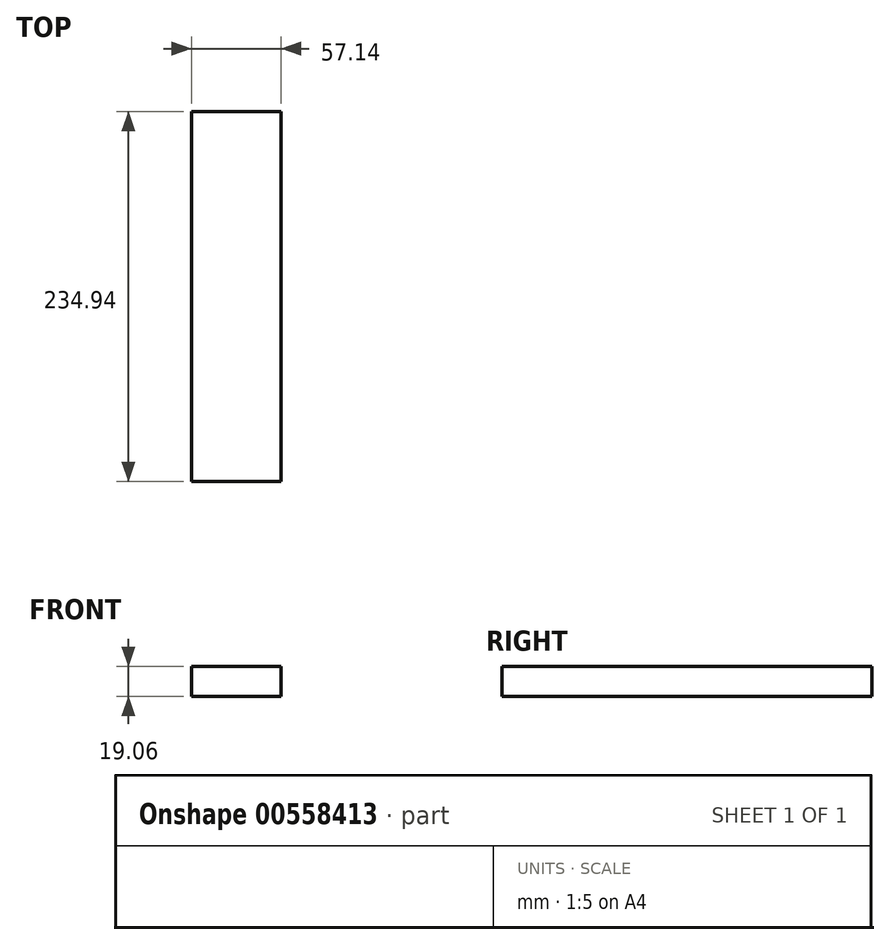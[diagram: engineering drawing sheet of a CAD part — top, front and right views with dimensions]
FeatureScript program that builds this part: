
annotation { "Feature Type Name" : "Feature", "Feature Type Description" : "" }
export const myFeature = defineFeature(function(context is Context, id is Id, definition is map)
    precondition{}
    {
        {
            var Q0;
            Q0=qCreatedBy(makeId("Top.planeOp"),FACE);
            var sketch = newSketch(context, id + "F0", { "sketchPlane" : qUnion([Q0])});
            skLineSegment(sketch, "E0.bottom", {"start": v(28.58, 117.47) * mm, "end": v(-28.57, 117.47) * mm});
            skLineSegment(sketch, "E0.top", {"start": v(28.57, -117.48) * mm, "end": v(-28.58, -117.48) * mm});
            skLineSegment(sketch, "E0.left", {"start": v(28.58, 117.47) * mm, "end": v(28.57, -117.48) * mm});
            skLineSegment(sketch, "E0.right", {"start": v(-28.57, 117.47) * mm, "end": v(-28.58, -117.48) * mm});
            skPoint(sketch, "E0.middle", {"position": v(0, 0) * mm});
            skSolve(sketch);
        }
        {
            var Q0;
            Q0=makeQuery(id+"F0.imprint","IMPRINT",FACE,{"disambiguationData":[TD([[makeQuery(id+"F0.imprint","IMPRINT",EDGE,{"derivedFrom":sQuery(id+"F0.wireOp",EDGE,"E0.bottom")}),1.0]])]});
            extrude(context, id + "F1", {"entities" : qUnion([Q0]), "endBound" : BoundingType.SYMMETRIC, "depth" : 19.05 * mm, "offsetDistance" : 25.4 * mm});
        }
    });
